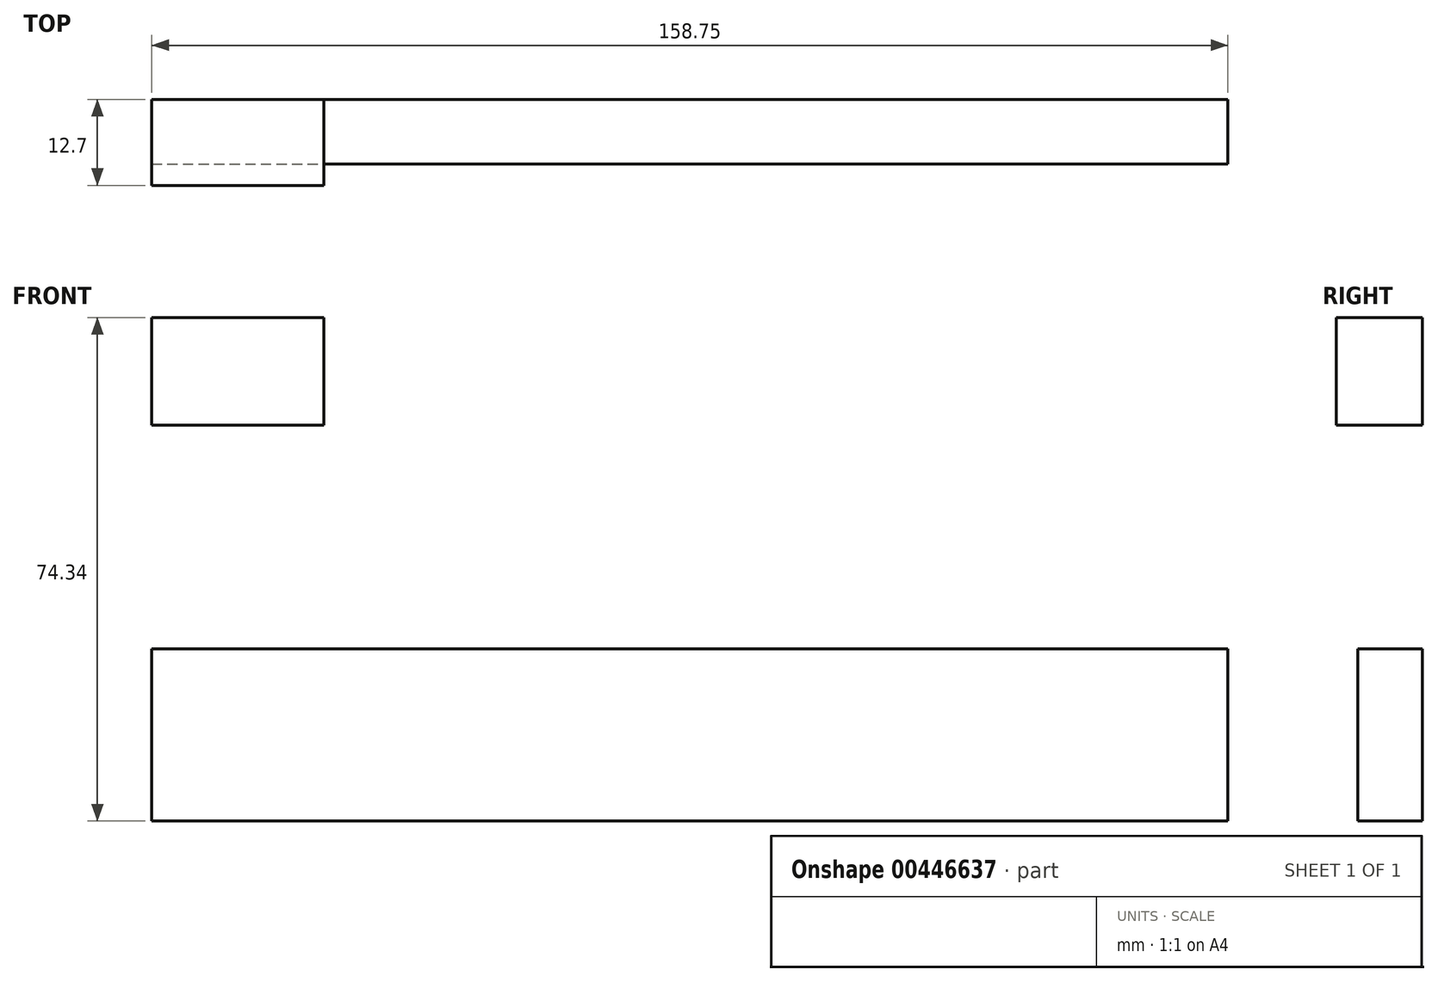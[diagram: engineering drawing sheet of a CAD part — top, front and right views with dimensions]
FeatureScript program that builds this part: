
annotation { "Feature Type Name" : "Feature", "Feature Type Description" : "" }
export const myFeature = defineFeature(function(context is Context, id is Id, definition is map)
    precondition{}
    {
        {
            var Q0;
            Q0=qCreatedBy(makeId("Front.planeOp"),FACE);
            var sketch = newSketch(context, id + "F0", { "sketchPlane" : qUnion([Q0])});
            skLineSegment(sketch, "E0.bottom", {"start": v(0, 0) * mm, "end": v(158.75, 0) * mm});
            skLineSegment(sketch, "E0.top", {"start": v(0, -25.4) * mm, "end": v(158.75, -25.4) * mm});
            skLineSegment(sketch, "E0.left", {"start": v(0, 0) * mm, "end": v(0, -25.4) * mm});
            skLineSegment(sketch, "E0.right", {"start": v(158.75, 0) * mm, "end": v(158.75, -25.4) * mm});
            skSolve(sketch);
        }
        {
            var Q0;
            Q0=makeQuery(id+"F0.imprint","IMPRINT",FACE,{"disambiguationData":[TD([[makeQuery(id+"F0.imprint","IMPRINT",EDGE,{"derivedFrom":sQuery(id+"F0.wireOp",EDGE,"E0.bottom")}),-1.0]])]});
            extrude(context, id + "F1", {"entities" : qUnion([Q0]), "depth" : 9.52 * mm});
        }
        {
            var Q0;
            Q0=qCreatedBy(makeId("Front.planeOp"),FACE);
            var sketch = newSketch(context, id + "F2", { "sketchPlane" : qUnion([Q0])});
            skPoint(sketch, "E1", {"position": v(0, 48.94) * mm});
            skLineSegment(sketch, "E2.bottom", {"start": v(0, 48.94) * mm, "end": v(25.4, 48.94) * mm});
            skLineSegment(sketch, "E2.top", {"start": v(0, 33.06) * mm, "end": v(25.4, 33.06) * mm});
            skLineSegment(sketch, "E2.left", {"start": v(0, 48.94) * mm, "end": v(0, 33.06) * mm});
            skLineSegment(sketch, "E2.right", {"start": v(25.4, 48.94) * mm, "end": v(25.4, 33.06) * mm});
            skSolve(sketch);
        }
        {
            var Q0;
            Q0=makeQuery(id+"F2.imprint","IMPRINT",FACE,{"disambiguationData":[TD([[makeQuery(id+"F2.imprint","IMPRINT",EDGE,{"derivedFrom":sQuery(id+"F2.wireOp",EDGE,"E2.bottom")}),-1.0]])]});
            extrude(context, id + "F3", {"entities" : qUnion([Q0]), "depth" : 12.7 * mm});
        }
    });
